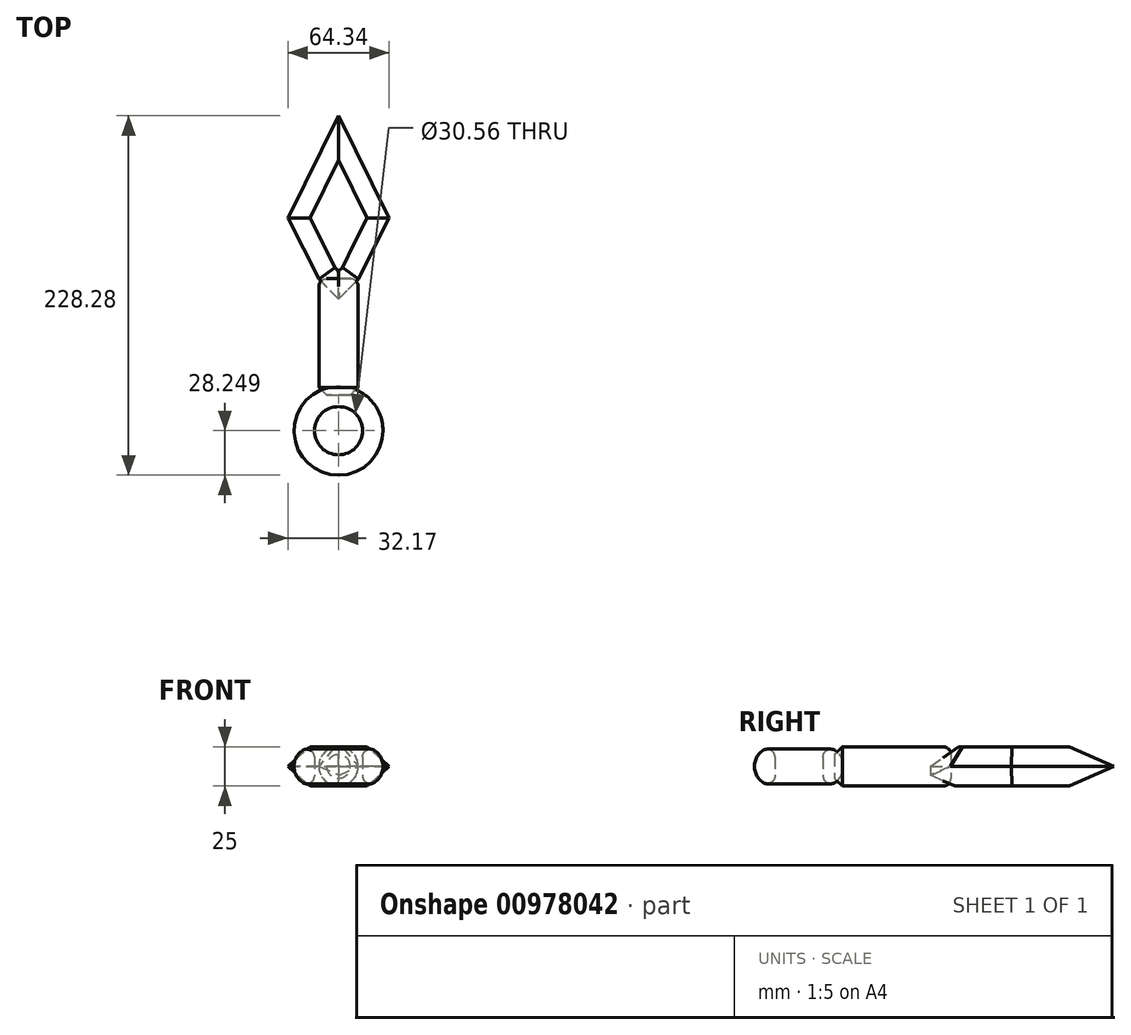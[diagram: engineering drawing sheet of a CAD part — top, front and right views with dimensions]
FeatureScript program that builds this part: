
annotation { "Feature Type Name" : "Feature", "Feature Type Description" : "" }
export const myFeature = defineFeature(function(context is Context, id is Id, definition is map)
    precondition{}
    {
        {
            var Q0;
            Q0=qCreatedBy(makeId("Top.planeOp"),FACE);
            var sketch = newSketch(context, id + "F0", { "sketchPlane" : qUnion([Q0])});
            skCircle(sketch, "E0", {"center": v(0, 0.14) * mm, "radius": 28.25 * mm});
            skCircle(sketch, "E1", {"center": v(0, 0.14) * mm, "radius": 15.28 * mm});
            skSolve(sketch);
        }
        {
            var Q0;
            Q0=makeQuery(id+"F0.imprint","IMPRINT",FACE,{"disambiguationData":[TD([[makeQuery(id+"F0.imprint","IMPRINT",EDGE,{"derivedFrom":sQuery(id+"F0.wireOp",EDGE,"E0")}),1.0]])]});
            extrude(context, id + "F1", {"entities" : qUnion([Q0]), "depth" : 12.5 * mm, "offsetDistance" : 25 * mm, "hasSecondDirection" : true, "secondDirectionOppositeDirection" : true, "secondDirectionDepth" : 12.5 * mm});
        }
        {
            var Q0;
            Q0=makeQuery(id+"F1.opExtrude","CAP_EDGE",EDGE,{"disambiguationData":[OSD([sQuery(id+"F0.wireOp",EDGE,"E0")])],"isStart":false});
            var Q1;
            Q1=makeQuery(id+"F1.opExtrude","CAP_EDGE",EDGE,{"disambiguationData":[OSD([sQuery(id+"F0.wireOp",EDGE,"E0")])],"isStart":true});
            fillet(context, id + "F2", {"entities" : qUnion([Q0, Q1]), "radius" : 12.5 * mm, "tangentPropagation" : true, "allowEdgeOverflow" : false});
        }
        {
            var Q0;
            Q0=makeQuery(id+"F1.opExtrude","CAP_EDGE",EDGE,{"disambiguationData":[OSD([sQuery(id+"F0.wireOp",EDGE,"E1")])],"isStart":false});
            var Q1;
            Q1=makeQuery(id+"F1.opExtrude","CAP_EDGE",EDGE,{"disambiguationData":[OSD([sQuery(id+"F0.wireOp",EDGE,"E1")])],"isStart":true});
            fillet(context, id + "F3", {"entities" : qUnion([Q0, Q1]), "radius" : 5 * mm, "tangentPropagation" : true, "allowEdgeOverflow" : false});
        }
        {
            var Q0;
            Q0=qCreatedBy(makeId("Top.planeOp"),FACE);
            var sketch = newSketch(context, id + "F4", { "sketchPlane" : qUnion([Q0])});
            skLineSegment(sketch, "E2.bottom", {"start": v(12.5, 22.7) * mm, "end": v(-12.5, 22.7) * mm});
            skLineSegment(sketch, "E2.top", {"start": v(12.5, 96.66) * mm, "end": v(-12.5, 96.66) * mm});
            skLineSegment(sketch, "E2.left", {"start": v(12.5, 22.7) * mm, "end": v(12.5, 96.66) * mm});
            skLineSegment(sketch, "E2.right", {"start": v(-12.5, 22.7) * mm, "end": v(-12.5, 96.66) * mm});
            skPoint(sketch, "E2.middle", {"position": v(0, 59.68) * mm});
            skLineSegment(sketch, "E3", {"start": v(0, 96.66) * mm, "end": v(0, 22.7) * mm});
            skSolve(sketch);
        }
        {
            var Q0;
            {var subQ0=sQuery(id+"F4.wireOp",EDGE,"E2.right");Q0=makeQuery(id+"F4.imprint","IMPRINT",FACE,{"disambiguationData":[TD([[makeQuery(id+"F4.imprint","IMPRINT",EDGE,{"derivedFrom":subQ0}),-1.0]])]});}
            var Q1;
            Q1=sQuery(id+"F4.wireOp",EDGE,"E3");
            revolve(context, id + "F5", {"surfaceOperationType" : NewSurfaceOperationType.NEW, "entities" : qUnion([Q0]), "axis" : qUnion([Q1]), "revolveType" : RevolveType.FULL});
        }
        {
            var Q0;
            Q0=makeQuery(id+"F5.opRevolve","SWEPT_EDGE",EDGE,{"disambiguationData":[OSD([sQuery(id+"F4.wireOp",EDGE,"E2.bottom"),sQuery(id+"F4.wireOp",EDGE,"E2.right")])]});
            chamfer(context, id + "F6", {"entities" : qUnion([Q0]), "width" : 5 * mm, "tangentPropagation" : true});
        }
        {
            var Q0;
            Q0=qCreatedBy(makeId("Top.planeOp"),FACE);
            var sketch = newSketch(context, id + "F7", { "sketchPlane" : qUnion([Q0])});
            skPoint(sketch, "E4.middle", {"position": v(0, 126.29) * mm});
            skLineSegment(sketch, "E5", {"start": v(-12.47, 96.48) * mm, "end": v(-21.11, 113.46) * mm});
            skLineSegment(sketch, "E6", {"start": v(21.11, 113.46) * mm, "end": v(12.7, 96.48) * mm});
            skLineSegment(sketch, "E7", {"start": v(-21.11, 113.46) * mm, "end": v(-32.17, 135.2) * mm});
            skLineSegment(sketch, "E8", {"start": v(-32.17, 135.2) * mm, "end": v(0, 200.17) * mm});
            skLineSegment(sketch, "E9", {"start": v(0, 200.17) * mm, "end": v(32.17, 135.2) * mm});
            skLineSegment(sketch, "E10", {"start": v(32.17, 135.2) * mm, "end": v(21.11, 113.46) * mm});
            skLineSegment(sketch, "E11", {"start": v(-12.47, 96.48) * mm, "end": v(0, 83.73) * mm});
            skLineSegment(sketch, "E12", {"start": v(0, 83.73) * mm, "end": v(12.7, 96.48) * mm});
            skSolve(sketch);
        }
        {
            var Q0;
            Q0=makeQuery(id+"F7.imprint","IMPRINT",FACE,{"disambiguationData":[TD([[makeQuery(id+"F7.imprint","IMPRINT",EDGE,{"derivedFrom":sQuery(id+"F7.wireOp",EDGE,"E5")}),-1.0]])]});
            extrude(context, id + "F8", {"entities" : qUnion([Q0]), "depth" : 12.5 * mm, "offsetDistance" : 25 * mm, "hasSecondDirection" : true, "secondDirectionOppositeDirection" : true, "secondDirectionDepth" : 12.5 * mm});
        }
        {
            var Q0;
            Q0=makeQuery(id+"F8.opExtrude","CAP_EDGE",EDGE,{"disambiguationData":[OSD([sQuery(id+"F7.wireOp",EDGE,"E6")])],"isStart":false});
            var Q1;
            Q1=makeQuery(id+"F8.opExtrude","CAP_FACE",FACE,{"disambiguationData":[OSD([sQuery(id+"F7.wireOp",EDGE,"E5"),sQuery(id+"F7.wireOp",EDGE,"E6"),sQuery(id+"F7.wireOp",EDGE,"E7"),sQuery(id+"F7.wireOp",EDGE,"E8"),sQuery(id+"F7.wireOp",EDGE,"E9"),sQuery(id+"F7.wireOp",EDGE,"E10"),sQuery(id+"F7.wireOp",EDGE,"E11"),sQuery(id+"F7.wireOp",EDGE,"E12")])],"isStart":false});
            var Q2;
            Q2=makeQuery(id+"F8.opExtrude","CAP_EDGE",EDGE,{"disambiguationData":[OSD([sQuery(id+"F7.wireOp",EDGE,"E9")])],"isStart":false});
            var Q3;
            Q3=makeQuery(id+"F8.opExtrude","CAP_EDGE",EDGE,{"disambiguationData":[OSD([sQuery(id+"F7.wireOp",EDGE,"E9")])],"isStart":true});
            var Q4;
            Q4=makeQuery(id+"F8.opExtrude","CAP_EDGE",EDGE,{"disambiguationData":[OSD([sQuery(id+"F7.wireOp",EDGE,"E8")])],"isStart":true});
            var Q5;
            Q5=makeQuery(id+"F8.opExtrude","CAP_EDGE",EDGE,{"disambiguationData":[OSD([sQuery(id+"F7.wireOp",EDGE,"E5"),sQuery(id+"F7.wireOp",EDGE,"E7")])],"isStart":true});
            var Q6;
            Q6=makeQuery(id+"F8.opExtrude","CAP_EDGE",EDGE,{"disambiguationData":[OSD([sQuery(id+"F7.wireOp",EDGE,"E6")])],"isStart":true});
            var Q7;
            Q7=makeQuery(id+"F8.opExtrude","CAP_EDGE",EDGE,{"disambiguationData":[OSD([sQuery(id+"F7.wireOp",EDGE,"E10")])],"isStart":true});
            chamfer(context, id + "F9", {"entities" : qUnion([Q0, Q1, Q2, Q3, Q4, Q5, Q6, Q7]), "width" : 12.5 * mm, "tangentPropagation" : true});
        }
        {
            var Q0;
            Q0=makeQuery(id+"F5.opRevolve","SWEPT_EDGE",EDGE,{"disambiguationData":[OSD([sQuery(id+"F4.wireOp",EDGE,"E2.top"),sQuery(id+"F4.wireOp",EDGE,"E2.right")])]});
            fillet(context, id + "F10", {"entities" : qUnion([Q0]), "radius" : 5 * mm, "tangentPropagation" : true, "allowEdgeOverflow" : false});
        }
    });
